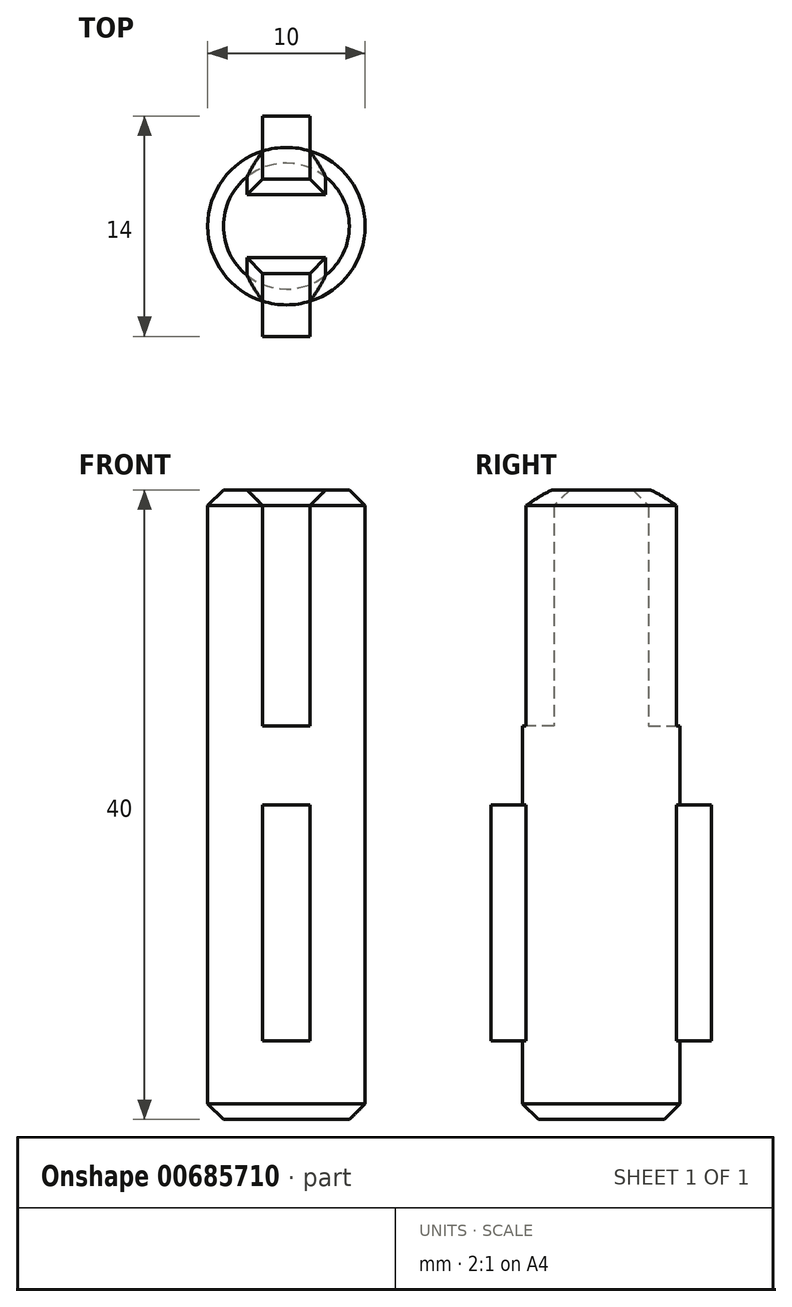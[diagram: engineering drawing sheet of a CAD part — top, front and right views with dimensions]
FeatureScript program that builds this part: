
annotation { "Feature Type Name" : "Feature", "Feature Type Description" : "" }
export const myFeature = defineFeature(function(context is Context, id is Id, definition is map)
    precondition{}
    {
        {
            var Q0;
            Q0=qCreatedBy(makeId("Top.planeOp"),FACE);
            var sketch = newSketch(context, id + "F0", { "sketchPlane" : qUnion([Q0])});
            skCircle(sketch, "E0", {"center": v(0, 0) * mm, "radius": 5 * mm});
            skSolve(sketch);
        }
        {
            var Q0;
            Q0=makeQuery(id+"F0.imprint","IMPRINT",FACE,{"disambiguationData":[TD([[makeQuery(id+"F0.imprint","IMPRINT",EDGE,{"derivedFrom":sQuery(id+"F0.wireOp",EDGE,"E0")}),1.0]])]});
            extrude(context, id + "F1", {"entities" : qUnion([Q0]), "depth" : 5 * mm, "offsetDistance" : 25 * mm});
        }
        {
            var Q0;
            Q0=makeQuery(id+"F1.opExtrude","CAP_FACE",FACE,{"disambiguationData":[OSD([sQuery(id+"F0.wireOp",EDGE,"E0")])],"isStart":false});
            var sketch = newSketch(context, id + "F2", { "sketchPlane" : qUnion([Q0])});
            skArc(sketch, "E1", {"start": v(-1.5, 4.77) * mm, "mid": v(-5, 0) * mm, "end": v(-1.5, -4.77) * mm});
            skLineSegment(sketch, "E2.bottom", {"start": v(1.5, 7) * mm, "end": v(-1.5, 7) * mm});
            skLineSegment(sketch, "E2.top", {"start": v(1.5, -7) * mm, "end": v(-1.5, -7) * mm});
            skLineSegment(sketch, "E2.left", {"start": v(1.5, 7) * mm, "end": v(1.5, 4.77) * mm});
            skLineSegment(sketch, "E2.right", {"start": v(-1.5, 7) * mm, "end": v(-1.5, 4.77) * mm});
            skLineSegment(sketch, "E3.trimOffspring", {"start": v(-1.5, -4.77) * mm, "end": v(-1.5, -7) * mm});
            skLineSegment(sketch, "E4.trimOffspring", {"start": v(1.5, -4.77) * mm, "end": v(1.5, -7) * mm});
            skArc(sketch, "E5.trimOffspring", {"start": v(1.5, -4.77) * mm, "mid": v(5, 0) * mm, "end": v(1.5, 4.77) * mm});
            skSolve(sketch);
        }
        {
            var Q0;
            Q0 = qSketchRegion(id + "F2", true);
            extrude(context, id + "F3", {"entities" : qUnion([Q0]), "operationType" : NewBodyOperationType.ADD, "depth" : 15 * mm, "offsetDistance" : 25 * mm});
        }
        {
            var Q0;
            Q0=makeQuery(id+"F3.opExtrude","CAP_FACE",FACE,{"disambiguationData":[OSD([sQuery(id+"F2.wireOp",EDGE,"E1"),sQuery(id+"F2.wireOp",EDGE,"E2.bottom"),sQuery(id+"F2.wireOp",EDGE,"E2.top"),sQuery(id+"F2.wireOp",EDGE,"E2.left"),sQuery(id+"F2.wireOp",EDGE,"E2.right"),sQuery(id+"F2.wireOp",EDGE,"E3.trimOffspring"),sQuery(id+"F2.wireOp",EDGE,"E4.trimOffspring"),sQuery(id+"F2.wireOp",EDGE,"E5.trimOffspring")])],"isStart":false});
            var sketch = newSketch(context, id + "F4", { "sketchPlane" : qUnion([Q0])});
            skCircle(sketch, "E6", {"center": v(0, 0) * mm, "radius": 5 * mm});
            skSolve(sketch);
        }
        {
            var Q0;
            {var subQ0=sQuery(id+"F4.wireOp",EDGE,"E6");var subQ1=makeQuery(id+"F4.imprint","INTERSECT",VERTEX,{"derivedFrom":[makeQuery(id+"F3.opExtrude","CAP_EDGE",EDGE,{"disambiguationData":[OSD([sQuery(id+"F2.wireOp",EDGE,"E2.right")])],"isStart":false}),subQ0]});Q0=makeQuery(id+"F4.imprint","IMPRINT",FACE,{"disambiguationData":[TD([[makeQuery(id+"F4.imprint","IMPRINT",EDGE,{"disambiguationData":[TD([[subQ1,1.0]])],"derivedFrom":subQ0}),1.0]])]});}
            extrude(context, id + "F5", {"entities" : qUnion([Q0]), "operationType" : NewBodyOperationType.ADD, "depth" : 5 * mm, "offsetDistance" : 25 * mm});
        }
        {
            var Q0;
            Q0=makeQuery(id+"F5.opExtrude","CAP_FACE",FACE,{"disambiguationData":[OSD([sQuery(id+"F4.wireOp",EDGE,"E6")])],"isStart":false});
            var sketch = newSketch(context, id + "F6", { "sketchPlane" : qUnion([Q0])});
            skArc(sketch, "E7", {"start": v(1.5, -4.77) * mm, "mid": v(5, 0) * mm, "end": v(1.5, 4.77) * mm});
            skLineSegment(sketch, "E8", {"start": v(0, 5) * mm, "end": v(0, -5) * mm, "construction": true});
            skLineSegment(sketch, "E9", {"start": v(-1.5, 3) * mm, "end": v(1.5, 3) * mm});
            skPoint(sketch, "E10", {"position": v(0, 3) * mm});
            skLineSegment(sketch, "E11", {"start": v(-1.5, 3) * mm, "end": v(-1.5, 4.77) * mm});
            skLineSegment(sketch, "E12", {"start": v(1.5, 3) * mm, "end": v(1.5, 4.77) * mm});
            skLineSegment(sketch, "E13", {"start": v(5, 0) * mm, "end": v(-5, 0) * mm, "construction": true});
            skLineSegment(sketch, "E14.MirrorCS", {"start": v(-1.5, -3) * mm, "end": v(1.5, -3) * mm});
            skLineSegment(sketch, "E15.MirrorCS", {"start": v(1.5, -3) * mm, "end": v(1.5, -4.77) * mm});
            skLineSegment(sketch, "E16.MirrorCS", {"start": v(-1.5, -3) * mm, "end": v(-1.5, -4.77) * mm});
            skArc(sketch, "E17.trimOffspring", {"start": v(-1.5, 4.77) * mm, "mid": v(-5, 0) * mm, "end": v(-1.5, -4.77) * mm});
            skSolve(sketch);
        }
        {
            var Q0;
            Q0 = qSketchRegion(id + "F6", true);
            extrude(context, id + "F7", {"entities" : qUnion([Q0]), "operationType" : NewBodyOperationType.ADD, "depth" : 15 * mm, "offsetDistance" : 25 * mm});
        }
        {
            var Q0;
            Q0=makeQuery(id+"F1.opExtrude","CAP_FACE",FACE,{"disambiguationData":[OSD([sQuery(id+"F0.wireOp",EDGE,"E0")])],"isStart":true});
            var Q1;
            Q1=makeQuery(id+"F7.opExtrude","CAP_FACE",FACE,{"disambiguationData":[OSD([sQuery(id+"F6.wireOp",EDGE,"E7"),sQuery(id+"F6.wireOp",EDGE,"E9"),sQuery(id+"F6.wireOp",EDGE,"E11"),sQuery(id+"F6.wireOp",EDGE,"E12"),sQuery(id+"F6.wireOp",EDGE,"E14.MirrorCS"),sQuery(id+"F6.wireOp",EDGE,"E15.MirrorCS"),sQuery(id+"F6.wireOp",EDGE,"E16.MirrorCS"),sQuery(id+"F6.wireOp",EDGE,"E17.trimOffspring")])],"isStart":false});
            chamfer(context, id + "F8", {"entities" : qUnion([Q0, Q1]), "width" : 1 * mm, "tangentPropagation" : true});
        }
    });
